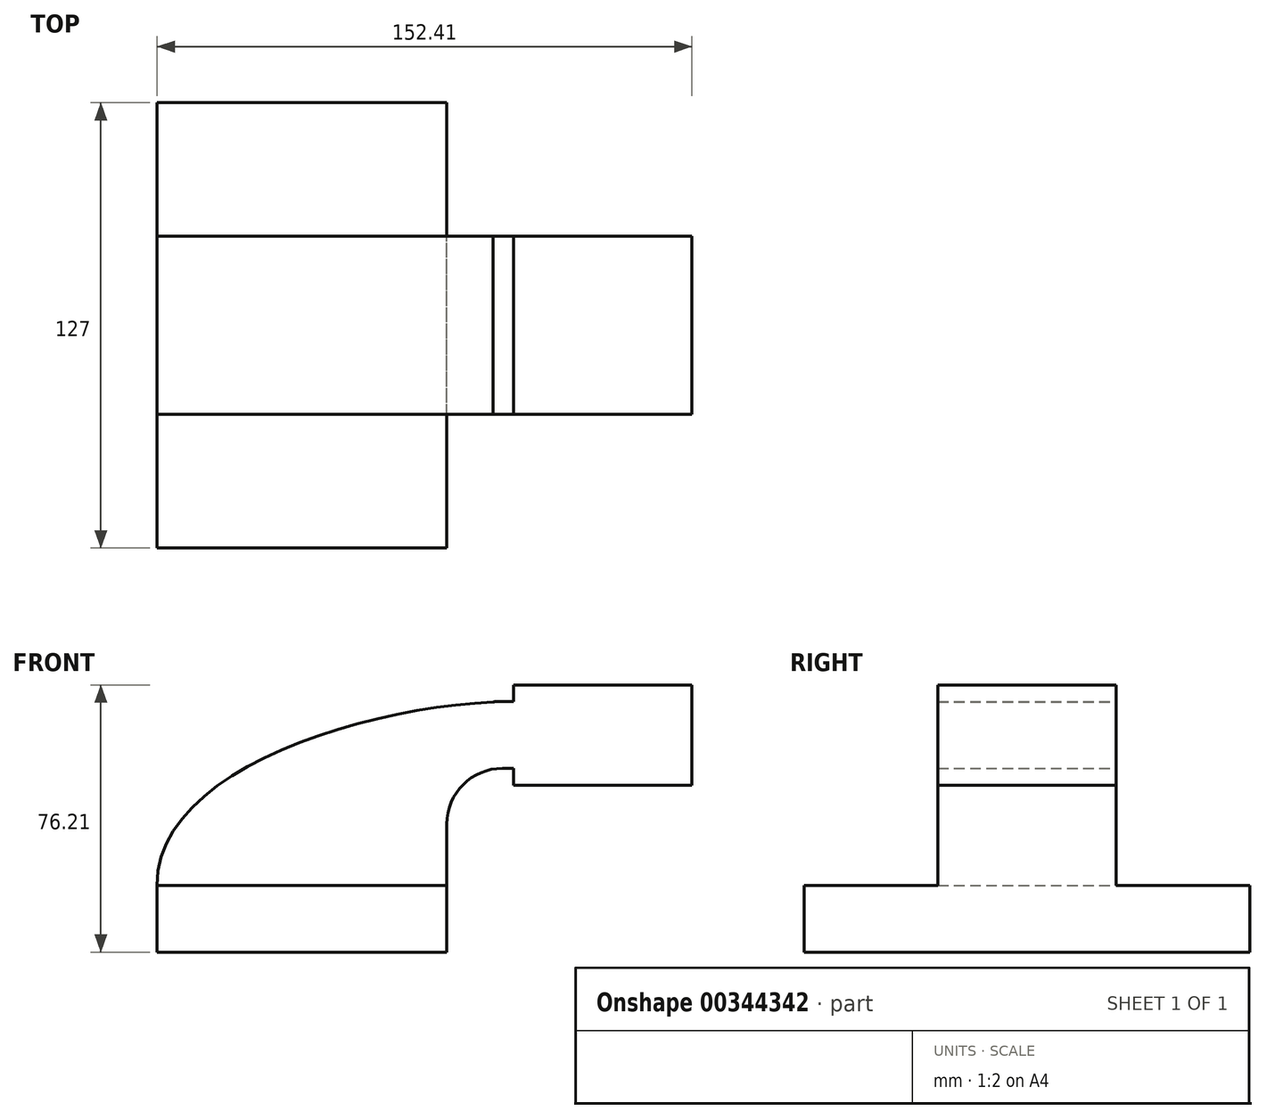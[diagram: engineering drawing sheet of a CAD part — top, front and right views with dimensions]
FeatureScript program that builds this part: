
annotation { "Feature Type Name" : "Feature", "Feature Type Description" : "" }
export const myFeature = defineFeature(function(context is Context, id is Id, definition is map)
    precondition{}
    {
        {
            var Q0;
            Q0=qCreatedBy(makeId("Front.planeOp"),FACE);
            var sketch = newSketch(context, id + "F0", { "sketchPlane" : qUnion([Q0])});
            skLineSegment(sketch, "E0.bottom", {"start": v(-41.28, 9.52) * mm, "end": v(41.28, 9.53) * mm});
            skLineSegment(sketch, "E0.top", {"start": v(-41.28, -9.53) * mm, "end": v(41.28, -9.53) * mm});
            skLineSegment(sketch, "E0.left", {"start": v(-41.28, 9.52) * mm, "end": v(-41.28, -9.53) * mm});
            skLineSegment(sketch, "E0.right", {"start": v(41.28, 9.53) * mm, "end": v(41.28, -9.52) * mm});
            skPoint(sketch, "E0.middle", {"position": v(0, 0) * mm});
            skLineSegment(sketch, "E1.bottom", {"start": v(111.12, 38.1) * mm, "end": v(60.32, 38.1) * mm});
            skLineSegment(sketch, "E1.top", {"start": v(111.12, 66.68) * mm, "end": v(60.32, 66.68) * mm});
            skLineSegment(sketch, "E1.left", {"start": v(111.12, 38.1) * mm, "end": v(111.12, 66.68) * mm});
            skLineSegment(sketch, "E1.right", {"start": v(60.32, 38.1) * mm, "end": v(60.32, 66.68) * mm});
            skPoint(sketch, "E1.middle", {"position": v(85.72, 52.39) * mm});
            skLineSegment(sketch, "E2", {"start": v(41.27, 9.53) * mm, "end": v(41.27, 27) * mm});
            skArc(sketch, "E3", {"start": v(41.27, 27) * mm, "mid": v(45.92, 38.23) * mm, "end": v(57.15, 42.88) * mm});
            skLineSegment(sketch, "E4", {"start": v(57.15, 42.88) * mm, "end": v(85.68, 42.88) * mm});
            skLineSegment(sketch, "E5.0", {"start": v(57.15, 61.93) * mm, "end": v(85.62, 61.93) * mm});
            skArc(sketch, "E5.1", {"start": v(22.22, 27) * mm, "mid": v(32.45, 51.7) * mm, "end": v(57.15, 61.93) * mm});
            skLineSegment(sketch, "E5.2", {"start": v(22.22, 9.53) * mm, "end": v(22.22, 27) * mm});
            skLineSegment(sketch, "E6", {"start": v(85.72, 38.1) * mm, "end": v(85.62, 66.68) * mm});
            skFitSpline(sketch, "E7", {"points": [v(-41.28, 9.52) * mm, v(57.15, 61.93) * mm], "startDerivative": vector(-1.43, 98.36) * mm, "endDerivative": vector(118.12, 3.48) * mm});
            skSolve(sketch);
        }
        {
            var Q0;
            Q0=makeQuery(id+"F0.imprint","IMPRINT",FACE,{"disambiguationData":[TD([[makeQuery(id+"F0.imprint","IMPRINT",EDGE,{"derivedFrom":sQuery(id+"F0.wireOp",EDGE,"E0.top")}),1.0]])]});
            extrude(context, id + "F1", {"entities" : qUnion([Q0]), "depth" : 63.5 * mm, "hasSecondDirection" : true, "secondDirectionOppositeDirection" : true, "secondDirectionDepth" : 63.5 * mm});
        }
        {
            var Q0;
            Q0 = qSketchRegion(id + "F0", true);
            extrude(context, id + "F2", {"entities" : qUnion([Q0]), "operationType" : NewBodyOperationType.ADD, "depth" : 25.4 * mm, "hasSecondDirection" : true, "secondDirectionOppositeDirection" : true, "secondDirectionDepth" : 25.4 * mm});
        }
    });
